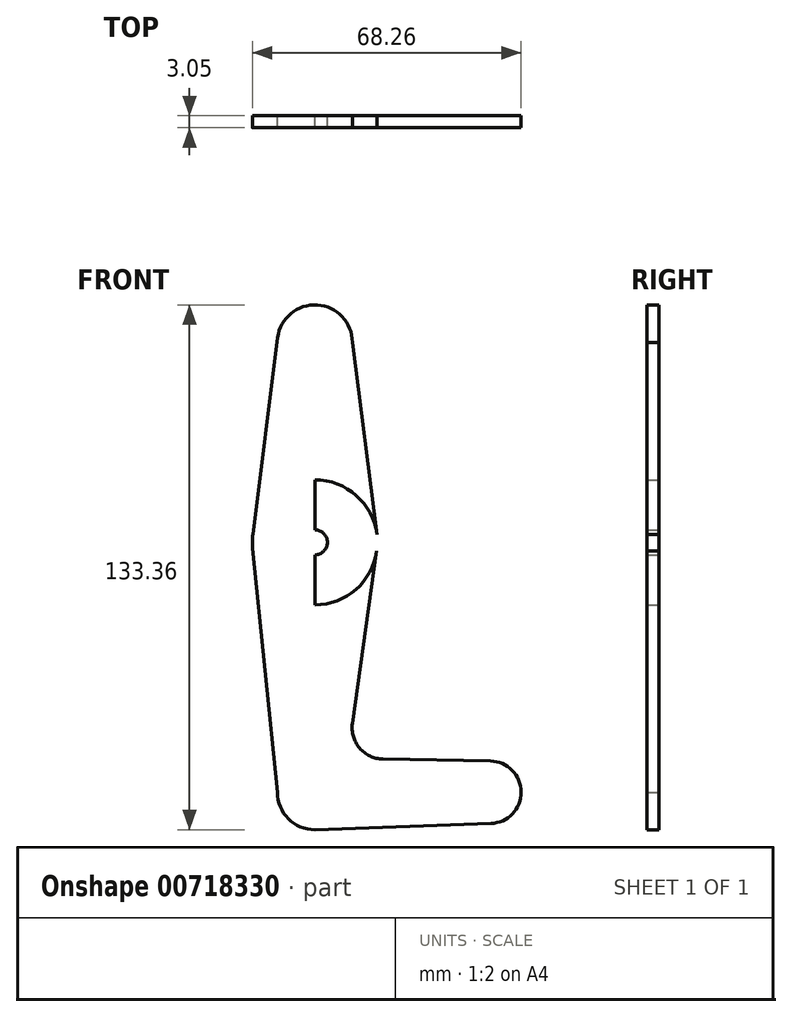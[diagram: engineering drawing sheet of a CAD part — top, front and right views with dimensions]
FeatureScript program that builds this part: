
annotation { "Feature Type Name" : "Feature", "Feature Type Description" : "" }
export const myFeature = defineFeature(function(context is Context, id is Id, definition is map)
    precondition{}
    {
        {
            var Q0;
            Q0=qCreatedBy(makeId("Front.planeOp"),FACE);
            var sketch = newSketch(context, id + "F0", { "sketchPlane" : qUnion([Q0])});
            skLineSegment(sketch, "E0", {"start": v(0, 0) * mm, "end": v(0, 114.3) * mm});
            skLineSegment(sketch, "E1", {"start": v(0, 0) * mm, "end": v(44.45, 0) * mm});
            skLineSegment(sketch, "E2", {"start": v(0, 0) * mm, "end": v(0, 63.5) * mm});
            skCircle(sketch, "E3", {"center": v(0, 63.5) * mm, "radius": 15.88 * mm});
            skCircle(sketch, "E4", {"center": v(0, 114.3) * mm, "radius": 9.53 * mm});
            skCircle(sketch, "E5", {"center": v(0, 0) * mm, "radius": 9.52 * mm});
            skCircle(sketch, "E6", {"center": v(44.45, 0) * mm, "radius": 7.94 * mm});
            skLineSegment(sketch, "E7", {"start": v(-9.45, 115.5) * mm, "end": v(-15.75, 65.48) * mm});
            skLineSegment(sketch, "E8", {"start": v(9.53, 114.3) * mm, "end": v(15.75, 65.5) * mm});
            skLineSegment(sketch, "E9", {"start": v(9.53, 17.5) * mm, "end": v(15.75, 61.48) * mm});
            skLineSegment(sketch, "E10", {"start": v(0, -9.52) * mm, "end": v(44.73, -7.93) * mm});
            skLineSegment(sketch, "E11", {"start": v(17.26, 8.43) * mm, "end": v(44.6, 7.94) * mm});
            skCircle(sketch, "E12", {"center": v(0, 114.3) * mm, "radius": 3.18 * mm});
            skCircle(sketch, "E13", {"center": v(0, 63.5) * mm, "radius": 3.18 * mm});
            skCircle(sketch, "E14", {"center": v(0, 0) * mm, "radius": 3.18 * mm});
            skCircle(sketch, "E15", {"center": v(44.45, 0) * mm, "radius": 3.18 * mm});
            skArc(sketch, "E16.filletArc", {"start": v(9.53, 17.5) * mm, "mid": v(11.36, 11.22) * mm, "end": v(17.26, 8.43) * mm});
            skLineSegment(sketch, "E17", {"start": v(-9.52, 0) * mm, "end": v(-15.8, 61.9) * mm});
            skCircle(sketch, "E18", {"center": v(-3.18, 100.03) * mm, "radius": 3.18 * mm});
            skSolve(sketch);
        }
        {
            var Q0;
            Q0=makeQuery(id+"F0.imprint","IMPRINT",FACE,{"disambiguationData":[TD([[makeQuery(id+"F0.imprint","IMPRINT",EDGE,{"derivedFrom":sQuery(id+"F0.wireOp",EDGE,"E12")}),-1.0]])]});
            var Q1;
            {var subQ12=sQuery(id+"F0.wireOp",EDGE,"E11");Q1=makeQuery(id+"F0.imprint","IMPRINT",FACE,{"disambiguationData":[TD([[makeQuery(id+"F0.imprint","IMPRINT",EDGE,{"derivedFrom":subQ12}),-1.0]])]});}
            var Q2;
            {var subQ3=sQuery(id+"F0.wireOp",EDGE,"E13");var subQ4=sQuery(id+"F0.wireOp",EDGE,"E0");var subQ5=makeQuery(id+"F0.imprint","INTERSECT",VERTEX,{"derivedFrom":[subQ4,subQ3]});Q2=makeQuery(id+"F0.imprint","IMPRINT",FACE,{"disambiguationData":[TD([[makeQuery(id+"F0.imprint","IMPRINT",EDGE,{"disambiguationData":[TD([[subQ5,-1.0]])],"derivedFrom":subQ4}),1.0]])]});}
            var Q3;
            {var subQ0=sQuery(id+"F0.wireOp",EDGE,"E8");Q3=makeQuery(id+"F0.imprint","IMPRINT",FACE,{"disambiguationData":[TD([[makeQuery(id+"F0.imprint","IMPRINT",EDGE,{"derivedFrom":subQ0}),-1.0]])]});}
            var Q4;
            Q4=makeQuery(id+"F0.imprint","IMPRINT",FACE,{"disambiguationData":[TD([[makeQuery(id+"F0.imprint","IMPRINT",EDGE,{"derivedFrom":sQuery(id+"F0.wireOp",EDGE,"E15")}),-1.0]])]});
            var Q5;
            {var subQ0=sQuery(id+"F0.wireOp",EDGE,"E7");Q5=makeQuery(id+"F0.imprint","IMPRINT",FACE,{"disambiguationData":[TD([[makeQuery(id+"F0.imprint","IMPRINT",EDGE,{"derivedFrom":subQ0}),1.0]])]});}
            var Q6;
            {var subQ2=sQuery(id+"F0.wireOp",EDGE,"E0");var subQ4=sQuery(id+"F0.wireOp",EDGE,"E13");var subQ5=makeQuery(id+"F0.imprint","INTERSECT",VERTEX,{"derivedFrom":[subQ2,subQ4]});Q6=makeQuery(id+"F0.imprint","IMPRINT",FACE,{"disambiguationData":[TD([[makeQuery(id+"F0.imprint","IMPRINT",EDGE,{"disambiguationData":[TD([[subQ5,-1.0]])],"derivedFrom":subQ2}),-1.0]])]});}
            var Q7;
            {var subQ6=sQuery(id+"F0.wireOp",EDGE,"E14");var subQ8=sQuery(id+"F0.wireOp",EDGE,"E1");var subQ9=makeQuery(id+"F0.imprint","INTERSECT",VERTEX,{"derivedFrom":[subQ8,subQ6]});Q7=makeQuery(id+"F0.imprint","IMPRINT",FACE,{"disambiguationData":[TD([[makeQuery(id+"F0.imprint","IMPRINT",EDGE,{"disambiguationData":[TD([[subQ9,-1.0]])],"derivedFrom":subQ8}),-1.0]])]});}
            var Q8;
            {var subQ0=sQuery(id+"F0.wireOp",EDGE,"E6");var subQ1=sQuery(id+"F0.wireOp",EDGE,"E1");var subQ2=makeQuery(id+"F0.imprint","INTERSECT",VERTEX,{"derivedFrom":[subQ1,subQ0]});Q8=makeQuery(id+"F0.imprint","IMPRINT",FACE,{"disambiguationData":[TD([[makeQuery(id+"F0.imprint","IMPRINT",EDGE,{"disambiguationData":[TD([[subQ2,1.0]])],"derivedFrom":subQ1}),-1.0]])]});}
            var Q9;
            {var subQ5=sQuery(id+"F0.wireOp",EDGE,"E17");Q9=makeQuery(id+"F0.imprint","IMPRINT",FACE,{"disambiguationData":[TD([[makeQuery(id+"F0.imprint","IMPRINT",EDGE,{"derivedFrom":subQ5}),-1.0]])]});}
            var Q10;
            {var subQ0=sQuery(id+"F0.wireOp",EDGE,"E14");var subQ1=sQuery(id+"F0.wireOp",EDGE,"E1");var subQ2=makeQuery(id+"F0.imprint","INTERSECT",VERTEX,{"derivedFrom":[subQ1,subQ0]});Q10=makeQuery(id+"F0.imprint","IMPRINT",FACE,{"disambiguationData":[TD([[makeQuery(id+"F0.imprint","IMPRINT",EDGE,{"disambiguationData":[TD([[subQ2,-1.0]])],"derivedFrom":subQ1}),1.0]])]});}
            var Q11;
            {var subQ0=sQuery(id+"F0.wireOp",EDGE,"E10");var subQ1=sQuery(id+"F0.wireOp",EDGE,"E5");var subQ2=makeQuery(id+"F0.imprint","INTERSECT",VERTEX,{"disambiguationData":[OD(0.0)],"derivedFrom":[subQ1,subQ0]});Q11=makeQuery(id+"F0.imprint","IMPRINT",FACE,{"disambiguationData":[TD([[makeQuery(id+"F0.imprint","IMPRINT",EDGE,{"disambiguationData":[TD([[subQ2,-1.0]])],"derivedFrom":subQ1}),1.0]])]});}
            var Q12;
            Q12=makeQuery(id+"F0.imprint","IMPRINT",FACE,{"disambiguationData":[TD([[makeQuery(id+"F0.imprint","IMPRINT",EDGE,{"derivedFrom":sQuery(id+"F0.wireOp",EDGE,"E12")}),1.0]])]});
            var Q13;
            Q13=makeQuery(id+"F0.imprint","IMPRINT",FACE,{"disambiguationData":[TD([[makeQuery(id+"F0.imprint","IMPRINT",EDGE,{"derivedFrom":sQuery(id+"F0.wireOp",EDGE,"E15")}),1.0]])]});
            var Q14;
            Q14=makeQuery(id+"F0.imprint","IMPRINT",FACE,{"disambiguationData":[TD([[makeQuery(id+"F0.imprint","IMPRINT",EDGE,{"derivedFrom":sQuery(id+"F0.wireOp",EDGE,"E18")}),1.0]])]});
            var Q15;
            {var subQ0=sQuery(id+"F0.wireOp",EDGE,"E2");var subQ1=sQuery(id+"F0.wireOp",EDGE,"E0");var subQ2=makeQuery(id+"F0.imprint","INTERSECT",VERTEX,{"derivedFrom":[subQ1,subQ0]});Q15=makeQuery(id+"F0.imprint","IMPRINT",FACE,{"disambiguationData":[TD([[makeQuery(id+"F0.imprint","IMPRINT",EDGE,{"disambiguationData":[TD([[subQ2,-1.0]])],"derivedFrom":subQ1}),1.0]])]});}
            var Q16;
            {var subQ0=sQuery(id+"F0.wireOp",EDGE,"E2");var subQ1=sQuery(id+"F0.wireOp",EDGE,"E0");var subQ2=makeQuery(id+"F0.imprint","INTERSECT",VERTEX,{"derivedFrom":[subQ1,subQ0]});Q16=makeQuery(id+"F0.imprint","IMPRINT",FACE,{"disambiguationData":[TD([[makeQuery(id+"F0.imprint","IMPRINT",EDGE,{"disambiguationData":[TD([[subQ2,-1.0]])],"derivedFrom":subQ1}),-1.0]])]});}
            var Q17;
            {var subQ0=sQuery(id+"F0.wireOp",EDGE,"E2");var subQ1=sQuery(id+"F0.wireOp",EDGE,"E1");var subQ2=makeQuery(id+"F0.imprint","INTERSECT",VERTEX,{"derivedFrom":[subQ1,subQ0]});Q17=makeQuery(id+"F0.imprint","IMPRINT",FACE,{"disambiguationData":[TD([[makeQuery(id+"F0.imprint","IMPRINT",EDGE,{"disambiguationData":[TD([[subQ2,-1.0]])],"derivedFrom":subQ1}),1.0]])]});}
            var Q18;
            {var subQ0=sQuery(id+"F0.wireOp",EDGE,"E2");var subQ1=sQuery(id+"F0.wireOp",EDGE,"E1");var subQ2=makeQuery(id+"F0.imprint","INTERSECT",VERTEX,{"derivedFrom":[subQ1,subQ0]});Q18=makeQuery(id+"F0.imprint","IMPRINT",FACE,{"disambiguationData":[TD([[makeQuery(id+"F0.imprint","IMPRINT",EDGE,{"disambiguationData":[TD([[subQ2,-1.0]])],"derivedFrom":subQ1}),-1.0]])]});}
            var Q19;
            Q19=sQuery(id+"F0.wireOp",EDGE,"E1");
            var Q20;
            Q20=sQuery(id+"F0.wireOp",EDGE,"E2");
            var Q21;
            Q21=sQuery(id+"F0.wireOp",EDGE,"E3");
            var Q22;
            Q22=sQuery(id+"F0.wireOp",EDGE,"E5");
            var Q23;
            Q23=sQuery(id+"F0.wireOp",EDGE,"E6");
            var Q24;
            Q24=sQuery(id+"F0.wireOp",EDGE,"E8");
            var Q25;
            Q25=sQuery(id+"F0.wireOp",EDGE,"E9");
            var Q26;
            Q26=sQuery(id+"F0.wireOp",EDGE,"E16.filletArc");
            var Q27;
            Q27=sQuery(id+"F0.wireOp",EDGE,"E14");
            var Q28;
            Q28=sQuery(id+"F0.wireOp",EDGE,"E18");
            var Q29;
            Q29=sQuery(id+"F0.wireOp",EDGE,"E0");
            var Q30;
            Q30=sQuery(id+"F0.wireOp",EDGE,"E7");
            var Q31;
            Q31=sQuery(id+"F0.wireOp",EDGE,"E15");
            var Q32;
            Q32=sQuery(id+"F0.wireOp",EDGE,"E13");
            var Q33;
            Q33=sQuery(id+"F0.wireOp",EDGE,"E17");
            var Q34;
            Q34=sQuery(id+"F0.wireOp",EDGE,"E10");
            var Q35;
            Q35=sQuery(id+"F0.wireOp",EDGE,"E11");
            var Q36;
            Q36=sQuery(id+"F0.wireOp",EDGE,"E4");
            var Q37;
            Q37=sQuery(id+"F0.wireOp",EDGE,"E12");
            extrude(context, id + "F1", {"entities" : qUnion([Q0, Q1, Q2, Q3, Q4, Q5, Q6, Q7, Q8, Q9, Q10, Q11, Q12, Q13, Q14, Q15, Q16, Q17, Q18]), "surfaceEntities" : qUnion([Q19, Q20, Q21, Q22, Q23, Q24, Q25, Q26, Q27, Q28, Q29, Q30, Q31, Q32, Q33, Q34, Q35, Q36, Q37]), "depth" : 3.05 * mm, "offsetDistance" : 25.4 * mm});
        }
    });
